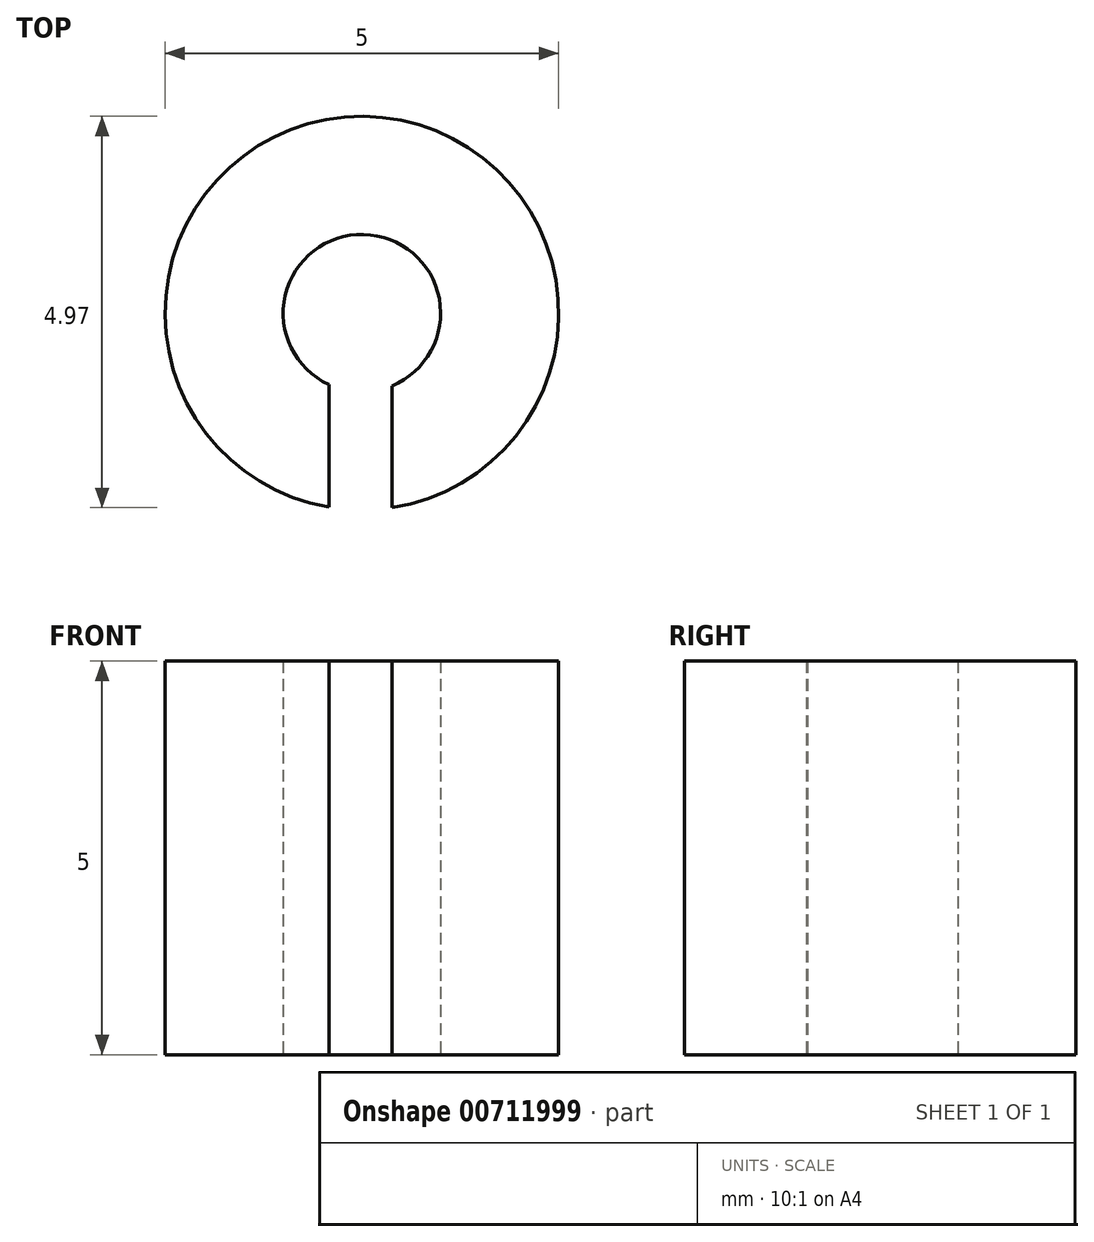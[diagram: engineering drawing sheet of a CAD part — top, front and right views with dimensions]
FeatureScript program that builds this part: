
annotation { "Feature Type Name" : "Feature", "Feature Type Description" : "" }
export const myFeature = defineFeature(function(context is Context, id is Id, definition is map)
    precondition{}
    {
        {
            var Q0;
            Q0=qCreatedBy(makeId("Top.planeOp"),FACE);
            var sketch = newSketch(context, id + "F0", { "sketchPlane" : qUnion([Q0])});
            skCircle(sketch, "E0", {"center": v(0, 0) * mm, "radius": 1 * mm});
            skCircle(sketch, "E1", {"center": v(0, 0) * mm, "radius": 2.5 * mm});
            skSolve(sketch);
        }
        {
            var Q0;
            Q0=qCreatedBy(makeId("Top.planeOp"),FACE);
            var sketch = newSketch(context, id + "F1", { "sketchPlane" : qUnion([Q0])});
            skLineSegment(sketch, "E2.bottom", {"start": v(-0.42, 0) * mm, "end": v(0.38, 0) * mm});
            skLineSegment(sketch, "E2.top", {"start": v(-0.42, -3.44) * mm, "end": v(0.38, -3.44) * mm});
            skLineSegment(sketch, "E2.left", {"start": v(-0.42, 0) * mm, "end": v(-0.42, -3.44) * mm});
            skLineSegment(sketch, "E2.right", {"start": v(0.38, 0) * mm, "end": v(0.38, -3.44) * mm});
            skSolve(sketch);
        }
        {
            var Q0;
            Q0 = qSketchRegion(id + "F0", true);
            extrude(context, id + "F2", {"entities" : qUnion([Q0]), "depth" : 5 * mm, "offsetDistance" : 25.4 * mm});
        }
        {
            var Q0;
            Q0 = qSketchRegion(id + "F1", true);
            extrude(context, id + "F3", {"entities" : qUnion([Q0]), "operationType" : NewBodyOperationType.REMOVE, "depth" : 25.4 * mm, "offsetDistance" : 25.4 * mm});
        }
    });
